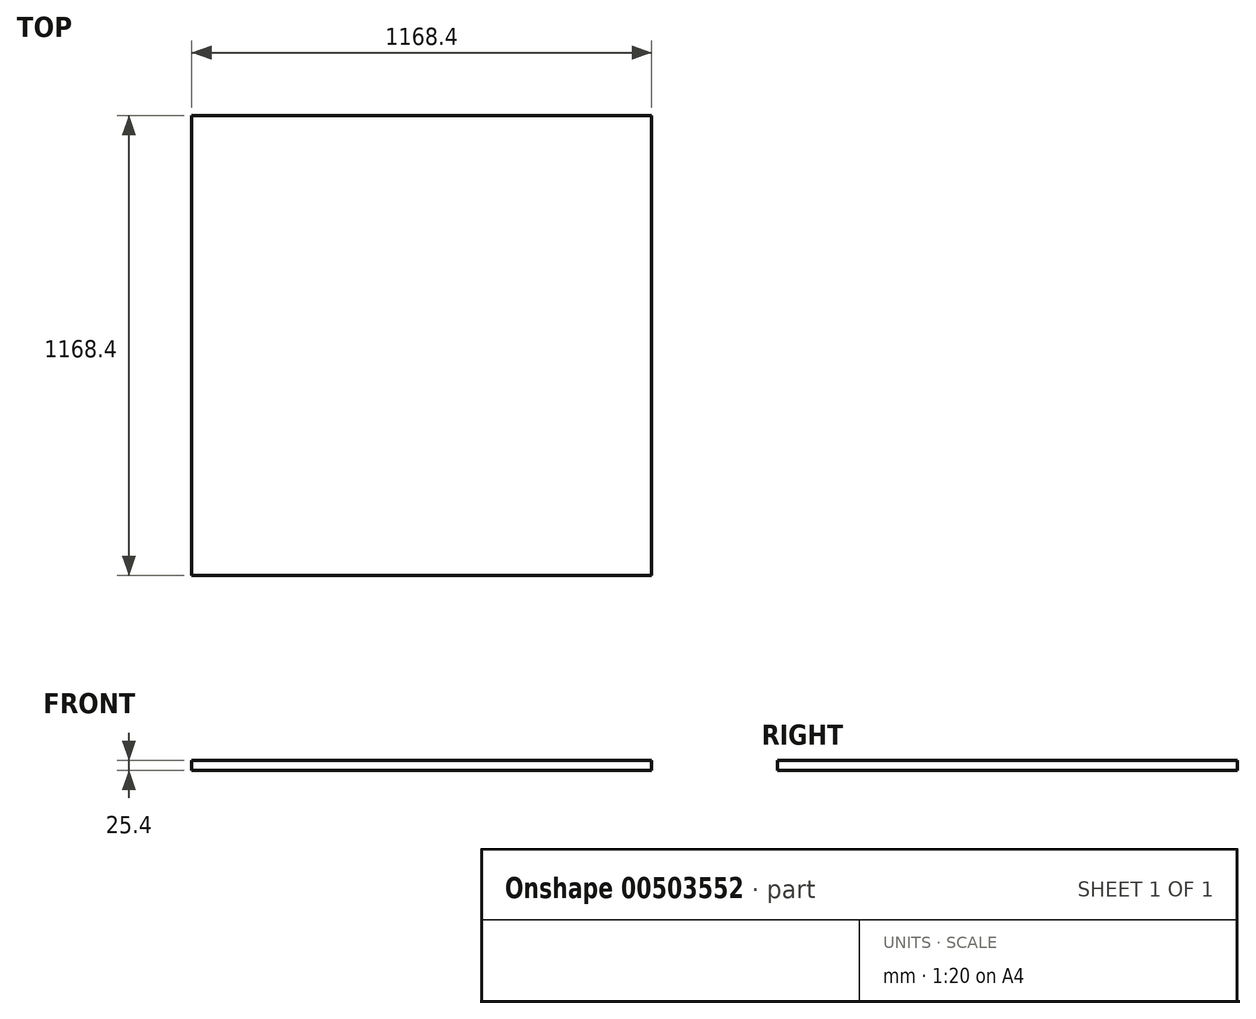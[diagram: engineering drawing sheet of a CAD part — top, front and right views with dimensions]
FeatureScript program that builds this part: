
annotation { "Feature Type Name" : "Feature", "Feature Type Description" : "" }
export const myFeature = defineFeature(function(context is Context, id is Id, definition is map)
    precondition{}
    {
        {
            var Q0;
            Q0=qCreatedBy(makeId("Top.planeOp"),FACE);
            var sketch = newSketch(context, id + "F0", { "sketchPlane" : qUnion([Q0])});
            skLineSegment(sketch, "E0.bottom", {"start": v(584.2, 584.2) * mm, "end": v(-584.2, 584.2) * mm});
            skLineSegment(sketch, "E0.top", {"start": v(584.2, -584.2) * mm, "end": v(-584.2, -584.2) * mm});
            skLineSegment(sketch, "E0.left", {"start": v(584.2, 584.2) * mm, "end": v(584.2, -584.2) * mm});
            skLineSegment(sketch, "E0.right", {"start": v(-584.2, 584.2) * mm, "end": v(-584.2, -584.2) * mm});
            skPoint(sketch, "E0.middle", {"position": v(0, 0) * mm});
            skSolve(sketch);
        }
        {
            var Q0;
            Q0=makeQuery(id+"F0.imprint","IMPRINT",FACE,{"disambiguationData":[TD([[makeQuery(id+"F0.imprint","IMPRINT",EDGE,{"derivedFrom":sQuery(id+"F0.wireOp",EDGE,"E0.bottom")}),1.0]])]});
            extrude(context, id + "F1", {"entities" : qUnion([Q0]), "endBound" : BoundingType.SYMMETRIC, "depth" : 25.4 * mm});
        }
    });
